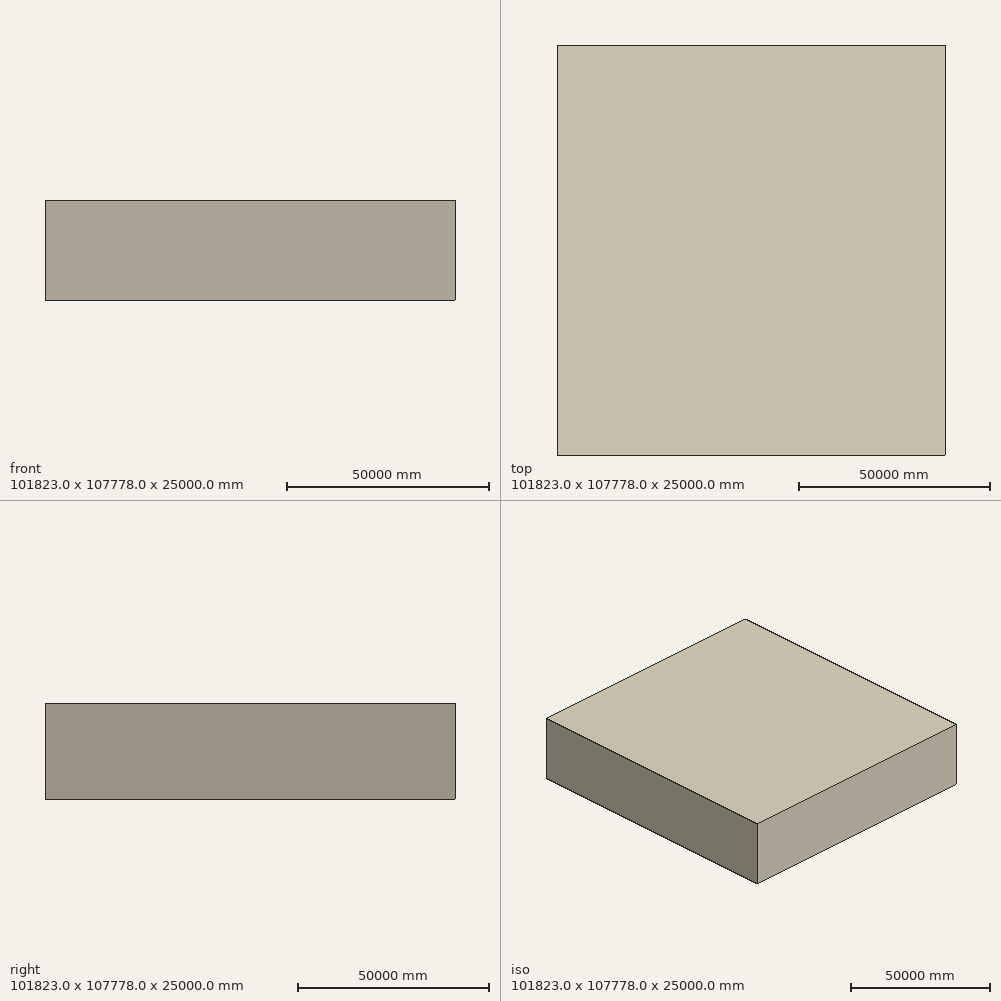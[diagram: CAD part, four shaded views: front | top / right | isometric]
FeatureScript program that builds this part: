
annotation { "Feature Type Name" : "Feature", "Feature Type Description" : "" }
export const myFeature = defineFeature(function(context is Context, id is Id, definition is map)
    precondition{}
    {
        {
            var Q0;
            Q0=qCreatedBy(makeId("Top.planeOp"),FACE);
            var sketch = newSketch(context, id + "F0", { "sketchPlane" : qUnion([Q0])});
            skLineSegment(sketch, "E0.bottom", {"start": v(50911.5, 53889) * mm, "end": v(-50911.5, 53889) * mm});
            skLineSegment(sketch, "E0.top", {"start": v(50911.5, -53889) * mm, "end": v(-50911.5, -53889) * mm});
            skLineSegment(sketch, "E0.left", {"start": v(50911.5, 53889) * mm, "end": v(50911.5, -53889) * mm});
            skLineSegment(sketch, "E0.right", {"start": v(-50911.5, 53889) * mm, "end": v(-50911.5, -53889) * mm});
            skPoint(sketch, "E0.middle", {"position": v(0, 0) * mm});
            skSolve(sketch);
        }
        {
            var Q0;
            Q0 = qSketchRegion(id + "F0", true);
            extrude(context, id + "F1", {"entities" : qUnion([Q0]), "oppositeDirection" : true, "depth" : 25000 * mm});
        }
    });
